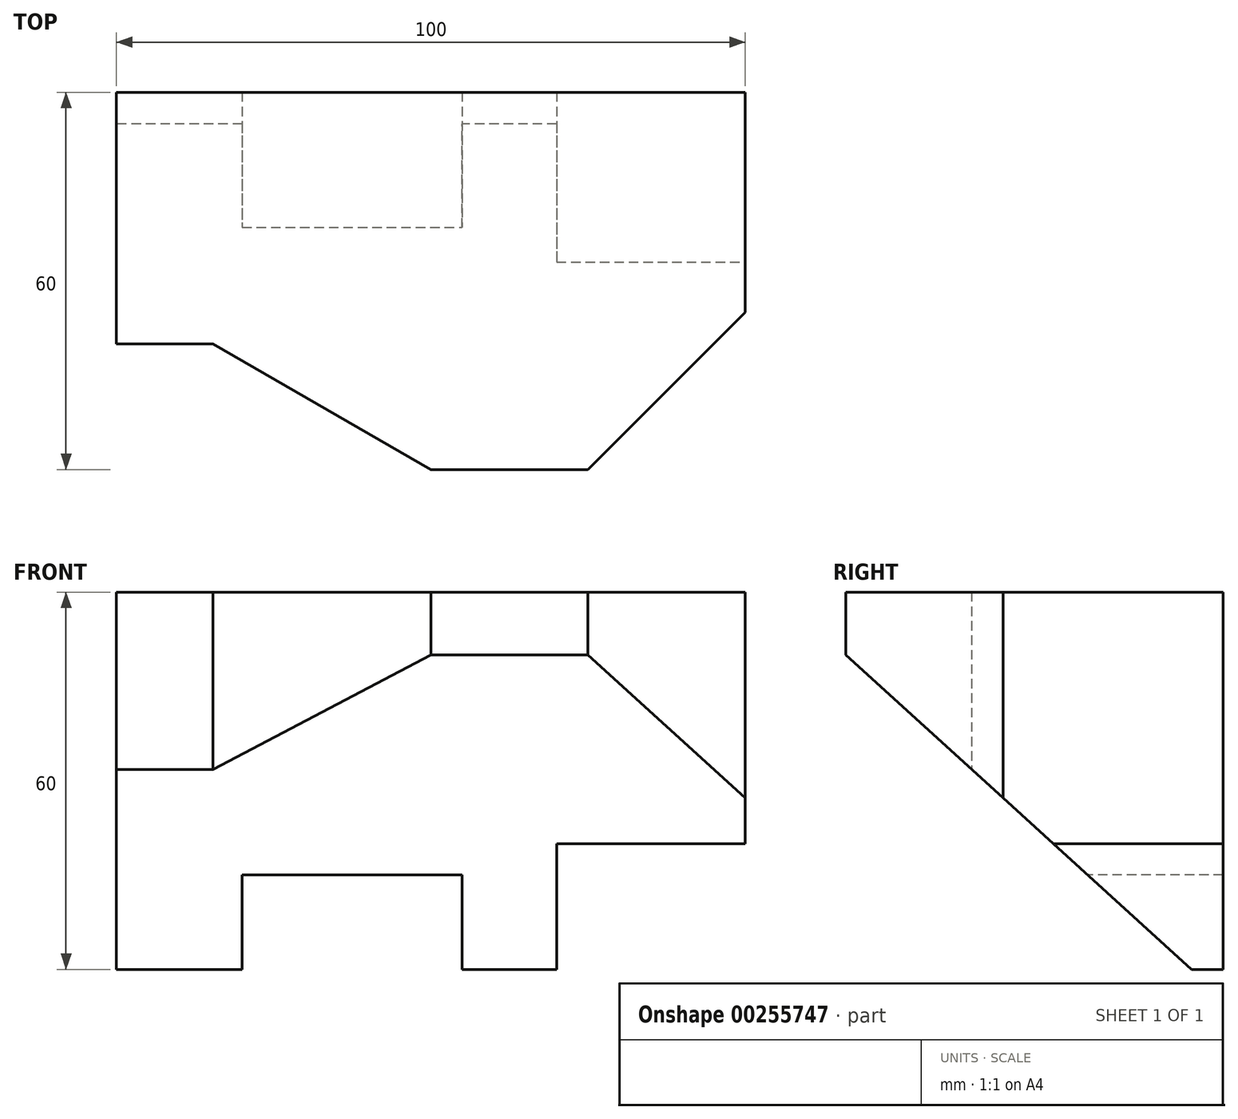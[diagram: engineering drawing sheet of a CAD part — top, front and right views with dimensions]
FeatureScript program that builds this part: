
annotation { "Feature Type Name" : "Feature", "Feature Type Description" : "" }
export const myFeature = defineFeature(function(context is Context, id is Id, definition is map)
    precondition{}
    {
        {
            var Q0;
            Q0=qCreatedBy(makeId("Front.planeOp"),FACE);
            var sketch = newSketch(context, id + "F0", { "sketchPlane" : qUnion([Q0])});
            skLineSegment(sketch, "E0", {"start": v(-55, 60) * mm, "end": v(-55, 0) * mm});
            skLineSegment(sketch, "E1", {"start": v(-55, 0) * mm, "end": v(-35, 0) * mm});
            skLineSegment(sketch, "E2", {"start": v(-35, 0) * mm, "end": v(-35, 15) * mm});
            skLineSegment(sketch, "E3", {"start": v(-35, 15) * mm, "end": v(0, 15) * mm});
            skLineSegment(sketch, "E4", {"start": v(0, 15) * mm, "end": v(0, 0) * mm});
            skLineSegment(sketch, "E5", {"start": v(0, 0) * mm, "end": v(15, 0) * mm});
            skLineSegment(sketch, "E6", {"start": v(15, 0) * mm, "end": v(15, 20) * mm});
            skLineSegment(sketch, "E7", {"start": v(15, 20) * mm, "end": v(45, 20) * mm});
            skLineSegment(sketch, "E8", {"start": v(45, 20) * mm, "end": v(45, 60) * mm});
            skLineSegment(sketch, "E9", {"start": v(45, 60) * mm, "end": v(-55, 60) * mm});
            skSolve(sketch);
        }
        {
            var Q0;
            Q0 = qSketchRegion(id + "F0", true);
            extrude(context, id + "F1", {"entities" : qUnion([Q0]), "oppositeDirection" : true, "depth" : 60 * mm});
        }
        {
            var Q0;
            Q0=makeQuery(id+"F1.opExtrude","SWEPT_FACE",FACE,{"disambiguationData":[OSD([sQuery(id+"F0.wireOp",EDGE,"E0")])]});
            var sketch = newSketch(context, id + "F2", { "sketchPlane" : qUnion([Q0])});
            skLineSegment(sketch, "E10", {"start": v(0, 50) * mm, "end": v(-55, 0) * mm});
            skLineSegment(sketch, "E11", {"start": v(-55, 0) * mm, "end": v(0, 0) * mm});
            skLineSegment(sketch, "E12", {"start": v(0, 0) * mm, "end": v(0, 50) * mm});
            skSolve(sketch);
        }
        {
            var Q0;
            Q0=makeQuery(id+"F2.imprint","IMPRINT",FACE,{"disambiguationData":[TD([[makeQuery(id+"F2.imprint","IMPRINT",EDGE,{"derivedFrom":sQuery(id+"F2.wireOp",EDGE,"E10")}),1.0]])]});
            extrude(context, id + "F3", {"entities" : qUnion([Q0]), "operationType" : NewBodyOperationType.REMOVE, "endBound" : BoundingType.THROUGH_ALL, "oppositeDirection" : true, "depth" : 25 * mm});
        }
        {
            var Q0;
            Q0=makeQuery(id+"F1.opExtrude","SWEPT_FACE",FACE,{"disambiguationData":[OSD([sQuery(id+"F0.wireOp",EDGE,"E7")])]});
            var sketch = newSketch(context, id + "F4", { "sketchPlane" : qUnion([Q0])});
            skLineSegment(sketch, "E13", {"start": v(-55, -20) * mm, "end": v(-39.64, -20) * mm});
            skLineSegment(sketch, "E14", {"start": v(-39.64, -20) * mm, "end": v(-5, 0) * mm});
            skLineSegment(sketch, "E15", {"start": v(-5, 0) * mm, "end": v(20, 0) * mm});
            skLineSegment(sketch, "E16", {"start": v(20, 0) * mm, "end": v(45, -25) * mm});
            skLineSegment(sketch, "E17", {"start": v(-55, -20) * mm, "end": v(-55, 0) * mm});
            skLineSegment(sketch, "E18", {"start": v(-55, 0) * mm, "end": v(-5, 0) * mm});
            skLineSegment(sketch, "E19", {"start": v(45, 0) * mm, "end": v(20, 0) * mm});
            skLineSegment(sketch, "E20", {"start": v(45, 0) * mm, "end": v(45, -25) * mm});
            skSolve(sketch);
        }
        {
            var Q0;
            Q0=makeQuery(id+"F4.imprint","IMPRINT",FACE,{"disambiguationData":[TD([[makeQuery(id+"F4.imprint","IMPRINT",EDGE,{"derivedFrom":sQuery(id+"F4.wireOp",EDGE,"E13")}),1.0]])]});
            var Q1;
            Q1=makeQuery(id+"F4.imprint","IMPRINT",FACE,{"disambiguationData":[TD([[makeQuery(id+"F4.imprint","IMPRINT",EDGE,{"derivedFrom":sQuery(id+"F4.wireOp",EDGE,"E16")}),1.0]])]});
            extrude(context, id + "F5", {"entities" : qUnion([Q0, Q1]), "operationType" : NewBodyOperationType.REMOVE, "endBound" : BoundingType.THROUGH_ALL, "oppositeDirection" : true, "depth" : 25 * mm});
        }
    });
